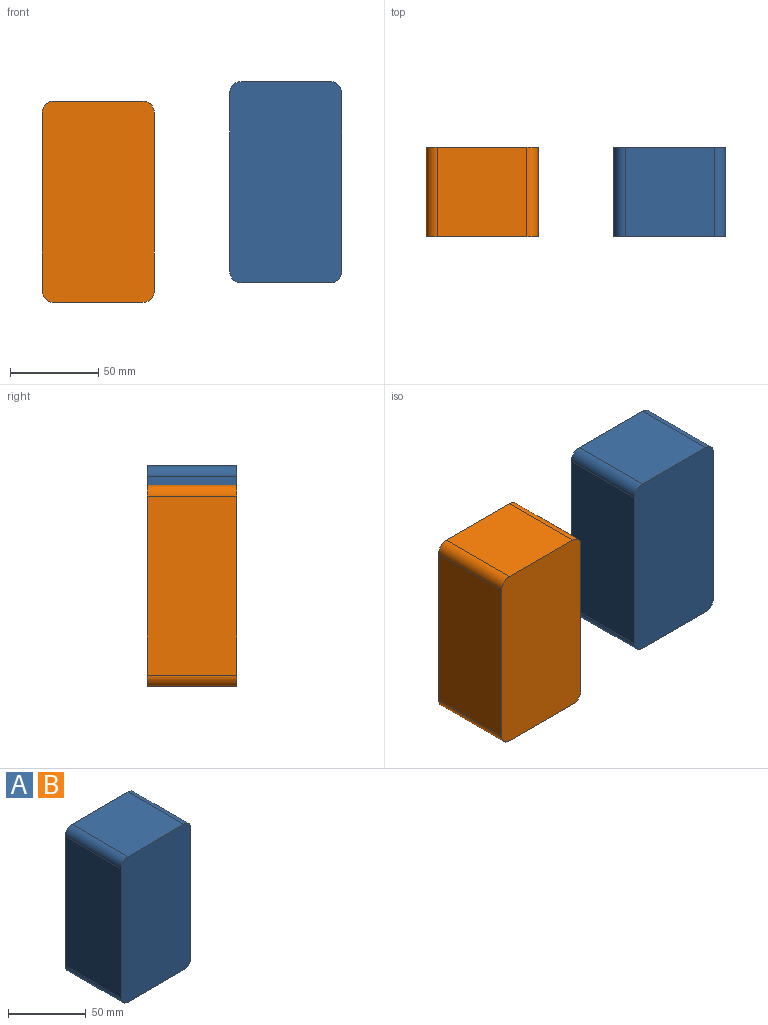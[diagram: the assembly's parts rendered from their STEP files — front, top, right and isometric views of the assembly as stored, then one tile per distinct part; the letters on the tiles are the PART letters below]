
ASSEMBLY  parts=2 mates=1
PART A: 10 faces, bbox 63.5x50.8x114.3 mm
  f0: cylinder r=6.35mm len=50.8mm, axis (0,1,0), area 506.7mm2, adj f1,f7,f8,f9
  f1: plane 50.8x50.8mm, normal (0,0,1), area 2580.6mm2, adj f0,f2,f8,f9
  f2: cylinder r=6.35mm len=50.8mm, axis (0,1,0), area 506.7mm2, adj f1,f3,f8,f9
  f3: plane 101.6x50.8mm, normal (-1,0,0), area 5161.3mm2, adj f2,f4,f8,f9
  f4: cylinder r=6.35mm len=50.8mm, axis (0,1,0), area 506.7mm2, adj f3,f5,f8,f9
  f5: plane 50.8x50.8mm, normal (0,0,-1), area 2580.6mm2, adj f4,f6,f8,f9
  f6: cylinder r=6.35mm len=50.8mm, axis (0,1,0), area 506.7mm2, adj f5,f7,f8,f9
  f7: plane 101.6x50.8mm, normal (1,0,0), area 5161.3mm2, adj f0,f6,f8,f9
  f8: plane 114.3x63.5mm, normal (0,-1,0), area 7223.4mm2, adj f0,f1,f2,f3,f4,f5,f6,f7
  f9: plane 114.3x63.5mm, normal (0,1,0), area 7223.4mm2, adj f0,f1,f2,f3,f4,f5,f6,f7
PART B: same geometry as A
PLACE A t=(73.59,-25.4,20.8)mm
PLACE B t=(-32.96,-25.4,9.73)mm
MATE planar B.f9 <-> A.f9  axis (0,1,0) through (-32.96,0,9.73)mm
